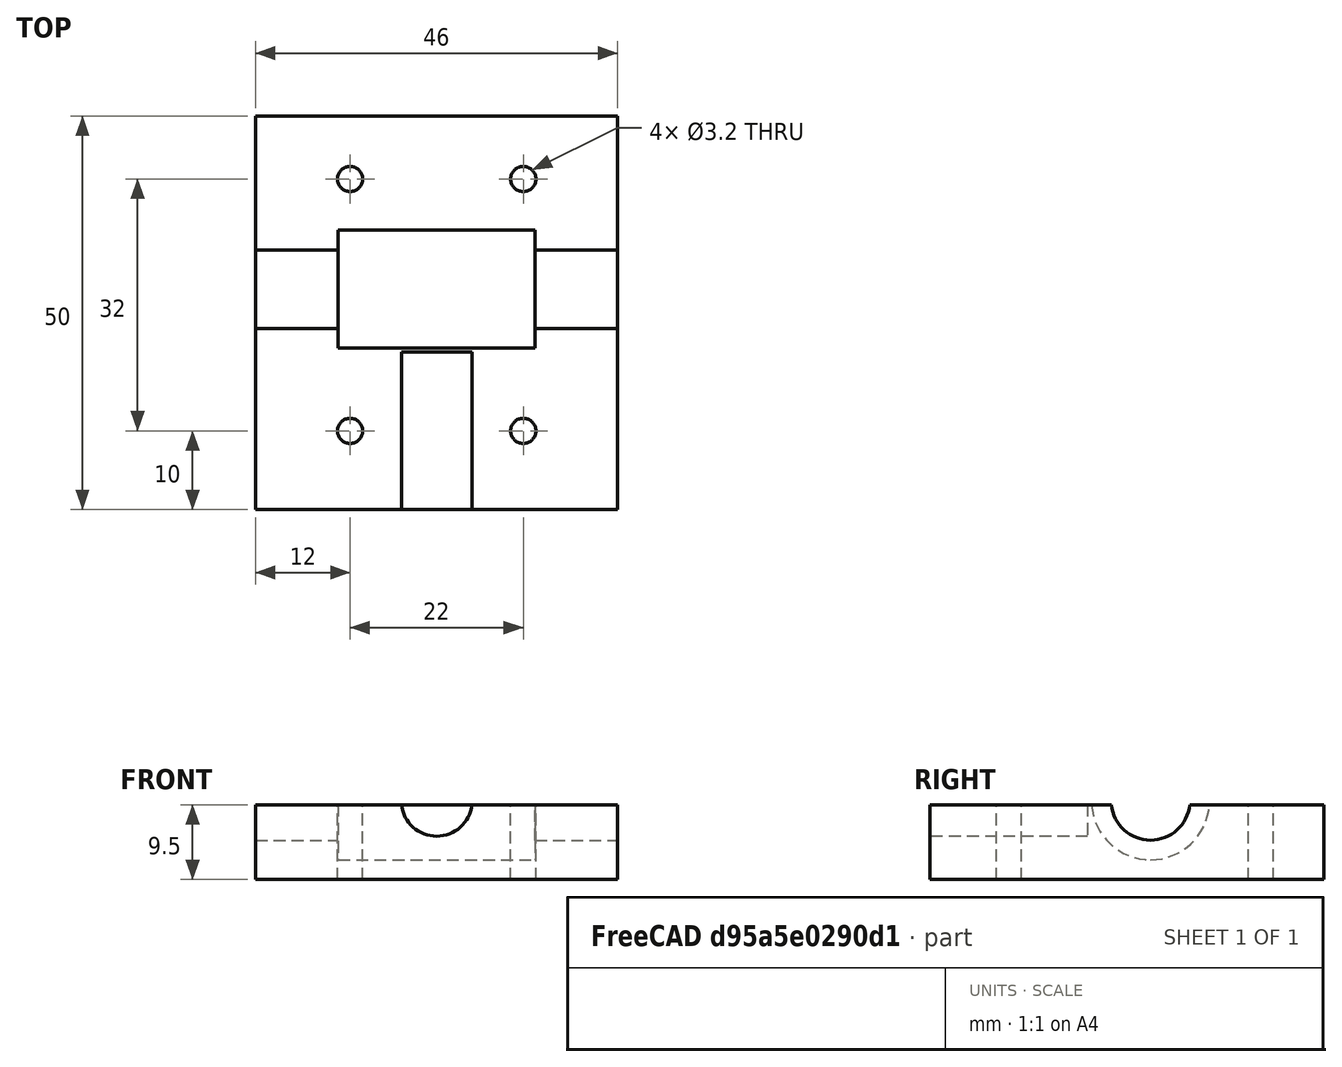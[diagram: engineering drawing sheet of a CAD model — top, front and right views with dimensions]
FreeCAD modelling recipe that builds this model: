
FCSTD DOCUMENT  (FreeCAD 0.14R3702 (Git))
Label: tapa_carro_eje_x
License: CC-BY 3.0
LicenseURL: http://creativecommons.org/licenses/by/3.0/
objects: Part::Cut×8, Part::Cylinder×7, Part::Box×2
note: 17 computed .brp shape members not serialized (recipe doc carries the construction recipe); baked Part::Feature solids carry a one-line shape summary decoded from their .brp

FEATURE [Part::Box] Box  label="Cubo"
  Height = 10
  Length = 46
  Width = 50
FEATURE [Part::Cylinder] Cylinder  label="Cilindro"
  Angle = 360
  Height = 10
  Placement = pos=(12,10,0) rot=(0,0,1;0rad)
  Radius = 1.6
FEATURE [Part::Cylinder] Cylinder001  label="Cilindro001"
  Angle = 360
  Height = 10
  Placement = pos=(34,10,0) rot=(0,0,1;0rad)
  Radius = 1.6
FEATURE [Part::Cylinder] Cylinder002  label="Cilindro002"
  Angle = 360
  Height = 10
  Placement = pos=(12,42,0) rot=(0,0,1;0rad)
  Radius = 1.6
FEATURE [Part::Cylinder] Cylinder003  label="Cilindro003"
  Angle = 360
  Height = 10
  Placement = pos=(34,42,0) rot=(0,0,1;0rad)
  Radius = 1.6
FEATURE [Part::Cut] Cut
  Base = -> Box
  Tool = -> Cylinder
FEATURE [Part::Cut] Cut001
  Base = -> Cut
  Tool = -> Cylinder001
FEATURE [Part::Cut] Cut002
  Base = -> Cut001
  Tool = -> Cylinder002
FEATURE [Part::Cut] Cut003
  Base = -> Cut002
  Tool = -> Cylinder003
FEATURE [Part::Cylinder] Cylinder004  label="Cilindro004"
  Angle = 360
  Height = 20
  Placement = pos=(23,20,10) rot=(1,0,0;1.5708rad)
  Radius = 4.5
FEATURE [Part::Cut] Cut004
  Base = -> Cut003
  Tool = -> Cylinder004
FEATURE [Part::Cylinder] Cylinder005  label="Cilindro005"
  Angle = 360
  Height = 46
  Placement = pos=(0,28,10) rot=(0,1,0;1.5708rad)
  Radius = 5
FEATURE [Part::Cut] Cut005
  Base = -> Cut004
  Tool = -> Cylinder005
FEATURE [Part::Cylinder] Cylinder006  label="Cilindro006"
  Angle = 360
  Height = 25
  Placement = pos=(10.5,28,10) rot=(0,1,0;1.5708rad)
  Radius = 7.5
FEATURE [Part::Cut] Cut006
  Base = -> Cut005
  Tool = -> Cylinder006
FEATURE [Part::Box] Box001  label="Cubo001"
  Height = 1
  Length = 46
  Placement = pos=(0,0,9.5) rot=(0,0,1;0rad)
  Width = 50
FEATURE [Part::Cut] Cut007
  Base = -> Cut006
  Tool = -> Box001
